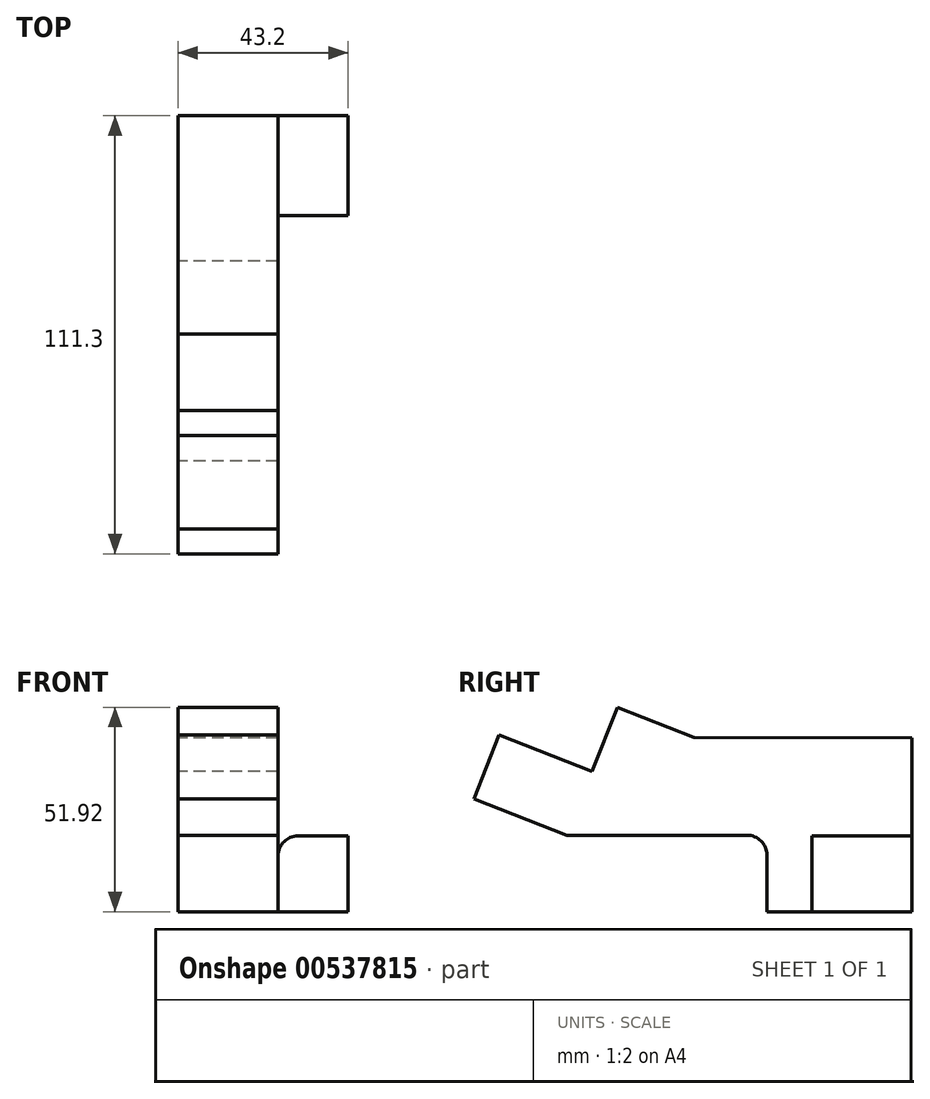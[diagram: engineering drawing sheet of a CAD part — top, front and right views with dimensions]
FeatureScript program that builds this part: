
annotation { "Feature Type Name" : "Feature", "Feature Type Description" : "" }
export const myFeature = defineFeature(function(context is Context, id is Id, definition is map)
    precondition{}
    {
        {
            var Q0;
            Q0=qCreatedBy(makeId("Right.planeOp"),FACE);
            var sketch = newSketch(context, id + "F0", { "sketchPlane" : qUnion([Q0])});
            skLineSegment(sketch, "E0", {"start": v(81.1, 44.28) * mm, "end": v(61.6, 51.92) * mm});
            skLineSegment(sketch, "E1", {"start": v(61.6, 51.92) * mm, "end": v(48.87, 19.45) * mm});
            skLineSegment(sketch, "E2", {"start": v(48.87, 19.45) * mm, "end": v(99.6, 19.45) * mm});
            skLineSegment(sketch, "E3", {"start": v(99.6, 19.45) * mm, "end": v(99.6, 0) * mm});
            skLineSegment(sketch, "E4", {"start": v(99.6, 0) * mm, "end": v(136.52, 0) * mm});
            skLineSegment(sketch, "E5", {"start": v(136.52, 0) * mm, "end": v(136.52, 44.15) * mm});
            skLineSegment(sketch, "E6", {"start": v(136.52, 44.15) * mm, "end": v(81.1, 44.28) * mm});
            skSolve(sketch);
        }
        {
            var Q0;
            Q0=makeQuery(id+"F0.imprint","IMPRINT",FACE,{"disambiguationData":[TD([[makeQuery(id+"F0.imprint","IMPRINT",EDGE,{"derivedFrom":sQuery(id+"F0.wireOp",EDGE,"E0")}),1.0]])]});
            extrude(context, id + "F1", {"entities" : qUnion([Q0]), "depth" : 25.4 * mm, "offsetDistance" : 25.4 * mm});
        }
        {
            var Q0;
            Q0=makeQuery(id+"F1.opExtrude","SWEPT_EDGE",EDGE,{"disambiguationData":[OSD([sQuery(id+"F0.wireOp",EDGE,"E2"),sQuery(id+"F0.wireOp",EDGE,"E3")])]});
            fillet(context, id + "F2", {"entities" : qUnion([Q0]), "radius" : 5.08 * mm, "tangentPropagation" : true, "allowEdgeOverflow" : false});
        }
        {
            var Q0;
            Q0=makeQuery(id+"F1.opExtrude","SWEPT_FACE",FACE,{"disambiguationData":[OSD([sQuery(id+"F0.wireOp",EDGE,"E1")])]});
            var sketch = newSketch(context, id + "F3", { "sketchPlane" : qUnion([Q0])});
            skLineSegment(sketch, "E7.bottom", {"start": v(25.4, 35.94) * mm, "end": v(0, 35.94) * mm});
            skLineSegment(sketch, "E7.top", {"start": v(25.4, 53.37) * mm, "end": v(0, 53.37) * mm});
            skLineSegment(sketch, "E7.left", {"start": v(25.4, 35.94) * mm, "end": v(25.4, 53.37) * mm});
            skLineSegment(sketch, "E7.right", {"start": v(0, 35.94) * mm, "end": v(0, 53.37) * mm});
            skSolve(sketch);
        }
        {
            var Q0;
            Q0=makeQuery(id+"F3.imprint","IMPRINT",FACE,{"disambiguationData":[TD([[makeQuery(id+"F3.imprint","IMPRINT",EDGE,{"derivedFrom":sQuery(id+"F3.wireOp",EDGE,"E7.bottom")}),-1.0]])]});
            extrude(context, id + "F4", {"entities" : qUnion([Q0]), "operationType" : NewBodyOperationType.ADD, "depth" : 25.4 * mm, "offsetDistance" : 25.4 * mm});
        }
        {
            var Q0;
            Q0=makeQuery(id+"F1.opExtrude","SWEPT_FACE",FACE,{"disambiguationData":[OSD([sQuery(id+"F0.wireOp",EDGE,"E5")])]});
            var sketch = newSketch(context, id + "F5", { "sketchPlane" : qUnion([Q0])});
            skLineSegment(sketch, "E8.bottom", {"start": v(-25.4, 0) * mm, "end": v(-43.2, 0) * mm});
            skLineSegment(sketch, "E8.top", {"start": v(-25.4, 19.27) * mm, "end": v(-43.2, 19.27) * mm});
            skLineSegment(sketch, "E8.left", {"start": v(-25.4, 0) * mm, "end": v(-25.4, 19.27) * mm});
            skLineSegment(sketch, "E8.right", {"start": v(-43.2, 0) * mm, "end": v(-43.2, 19.27) * mm});
            skSolve(sketch);
        }
        {
            var Q0;
            Q0=makeQuery(id+"F5.imprint","IMPRINT",FACE,{"disambiguationData":[TD([[makeQuery(id+"F5.imprint","IMPRINT",EDGE,{"derivedFrom":sQuery(id+"F5.wireOp",EDGE,"E8.bottom")}),-1.0]])]});
            extrude(context, id + "F6", {"entities" : qUnion([Q0]), "oppositeDirection" : true, "depth" : 25.4 * mm, "offsetDistance" : 25.4 * mm});
        }
        {
            var Q0;
            Q0=makeQuery(id+"F6.opExtrude","SWEPT_EDGE",EDGE,{"disambiguationData":[OSD([sQuery(id+"F0.wireOp",EDGE,"E5"),sQuery(id+"F5.wireOp",EDGE,"E8.top"),sQuery(id+"F5.wireOp",EDGE,"E8.left")])]});
            fillet(context, id + "F7", {"entities" : qUnion([Q0]), "radius" : 5.08 * mm, "tangentPropagation" : true, "allowEdgeOverflow" : false});
        }
    });
